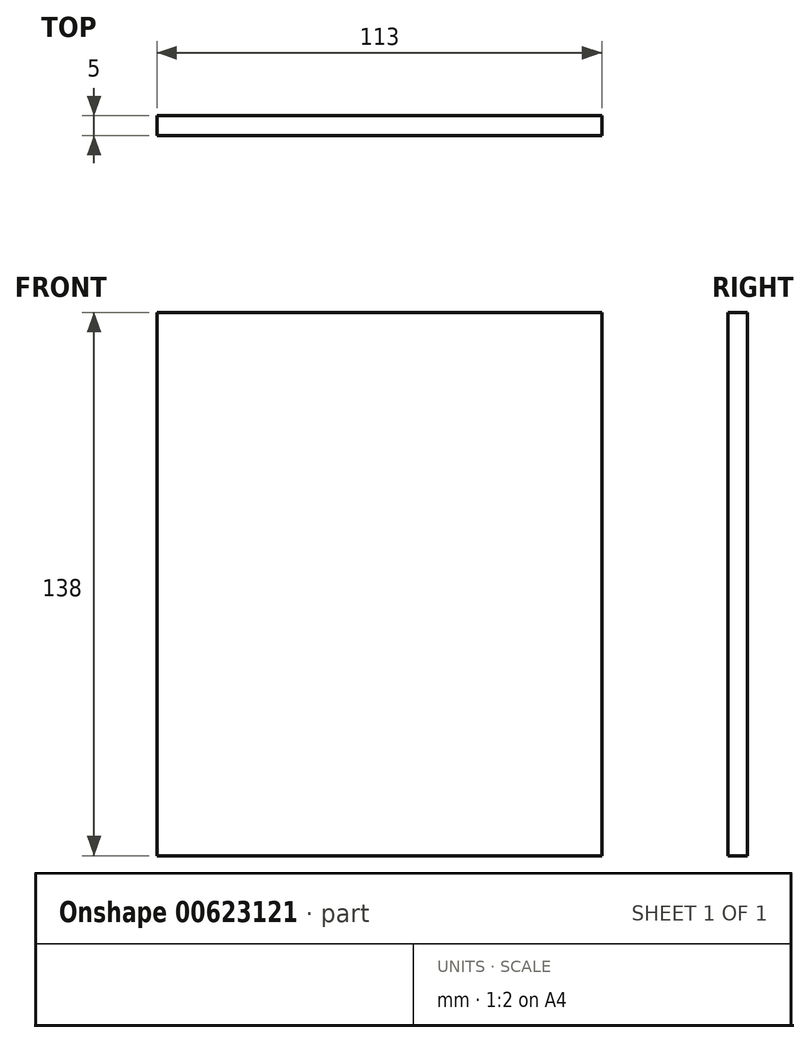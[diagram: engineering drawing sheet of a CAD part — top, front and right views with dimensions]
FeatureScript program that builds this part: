
annotation { "Feature Type Name" : "Feature", "Feature Type Description" : "" }
export const myFeature = defineFeature(function(context is Context, id is Id, definition is map)
    precondition{}
    {
        {
            var Q0;
            Q0=qCreatedBy(makeId("Front.planeOp"),FACE);
            var sketch = newSketch(context, id + "F0", { "sketchPlane" : qUnion([Q0])});
            skLineSegment(sketch, "E0.bottom", {"start": v(0, 0) * mm, "end": v(113, 0) * mm});
            skLineSegment(sketch, "E0.top", {"start": v(0, 138) * mm, "end": v(113, 138) * mm});
            skLineSegment(sketch, "E0.left", {"start": v(0, 0) * mm, "end": v(0, 138) * mm});
            skLineSegment(sketch, "E0.right", {"start": v(113, 0) * mm, "end": v(113, 138) * mm});
            skSolve(sketch);
        }
        {
            var Q0;
            Q0=makeQuery(id+"F0.imprint","IMPRINT",FACE,{"disambiguationData":[TD([[makeQuery(id+"F0.imprint","IMPRINT",EDGE,{"derivedFrom":sQuery(id+"F0.wireOp",EDGE,"E0.bottom")}),1.0]])]});
            extrude(context, id + "F1", {"entities" : qUnion([Q0]), "depth" : 5 * mm, "offsetDistance" : 25 * mm});
        }
    });
